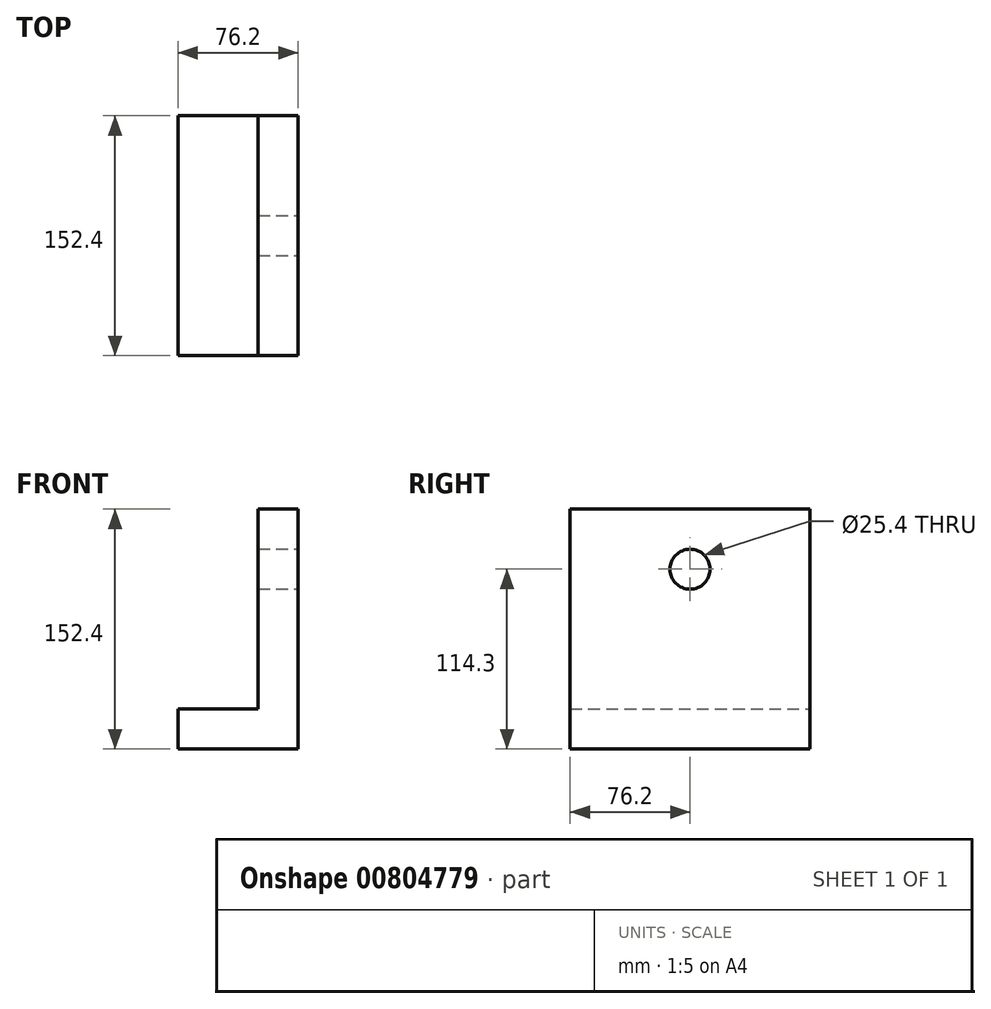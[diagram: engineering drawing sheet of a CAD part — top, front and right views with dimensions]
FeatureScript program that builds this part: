
annotation { "Feature Type Name" : "Feature", "Feature Type Description" : "" }
export const myFeature = defineFeature(function(context is Context, id is Id, definition is map)
    precondition{}
    {
        {
            var Q0;
            Q0=qCreatedBy(makeId("Front.planeOp"),FACE);
            var sketch = newSketch(context, id + "F0", { "sketchPlane" : qUnion([Q0])});
            skLineSegment(sketch, "E0", {"start": v(0, 0) * mm, "end": v(0, 152.4) * mm});
            skLineSegment(sketch, "E1", {"start": v(0, 0) * mm, "end": v(-76.2, 0) * mm});
            skLineSegment(sketch, "E2", {"start": v(-76.2, 0) * mm, "end": v(-76.2, 25.4) * mm});
            skLineSegment(sketch, "E3", {"start": v(-76.2, 25.4) * mm, "end": v(-25.4, 25.4) * mm});
            skLineSegment(sketch, "E4", {"start": v(-25.4, 25.4) * mm, "end": v(-25.4, 152.4) * mm});
            skLineSegment(sketch, "E5", {"start": v(0, 152.4) * mm, "end": v(-25.4, 152.4) * mm});
            skSolve(sketch);
        }
        {
            var Q0;
            Q0 = qSketchRegion(id + "F0", true);
            extrude(context, id + "F1", {"entities" : qUnion([Q0]), "endBound" : BoundingType.SYMMETRIC, "depth" : 152.4 * mm, "offsetDistance" : 25.4 * mm});
        }
        {
            var Q0;
            Q0=makeQuery(id+"F1.opExtrude","SWEPT_FACE",FACE,{"disambiguationData":[OSD([sQuery(id+"F0.wireOp",EDGE,"E0")])]});
            var sketch = newSketch(context, id + "F2", { "sketchPlane" : qUnion([Q0])});
            skCircle(sketch, "E6", {"center": v(0, 114.3) * mm, "radius": 12.7 * mm});
            skSolve(sketch);
        }
        {
            var Q0;
            Q0=makeQuery(id+"F2.imprint","IMPRINT",FACE,{"disambiguationData":[TD([[makeQuery(id+"F2.imprint","IMPRINT",EDGE,{"derivedFrom":sQuery(id+"F2.wireOp",EDGE,"E6")}),1.0]])]});
            extrude(context, id + "F3", {"entities" : qUnion([Q0]), "operationType" : NewBodyOperationType.REMOVE, "oppositeDirection" : true, "depth" : 25.4 * mm, "offsetDistance" : 25.4 * mm});
        }
    });
